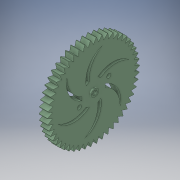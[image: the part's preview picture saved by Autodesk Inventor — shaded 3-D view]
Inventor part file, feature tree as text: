
AUTODESK INVENTOR PART (.ipt)
format: ipt  version: 2018 (Build 220112000, 112)  size: 389,632 bytes
history: native  units: in
note: dims shown in document units (in); Inventor stores cm internally (conversion verified against a paired STEP export)
features: sketch x5, extrude x4
ambient origin geometry x8: Origin, YZ Plane, XZ Plane, XY Plane, X Axis, Y Axis, Z Axis, Center Point
bodies: Solid1 (feature_tree), Solid2 (feature_tree)
feature tree (9):
  sketch  "Sketch1"  dims[d0=2.5591in d1=1.1811in]
  extrude  "Extrusion1"  Depth=1.1811in
  sketch  "Sketch2"  dims[d2=2.3622in d4=360.0deg d6=0.1575in]
  sketch  "Sketch3"  dims[d7=0.2362in d8=0.0in d9=19.685in d11=360.0deg]
  sketch  "Sketch4"  dims[d15=0.114in d16=0.114in]
  extrude  "Extrusion5"  Depth=0.1575in
  extrude  "Extrusion6"  Depth=0.2362in TaperAngle=360.0deg
  extrude  "Extrusion7"  Depth=0.114in
  sketch  "Sketch6"  dims[d24=0.2756in d25=0.0in d26=0.2756in d27=0.0in d28=0.118in d29=0.118in d30=0.045in d31=0.2756in d32=0.0in]
